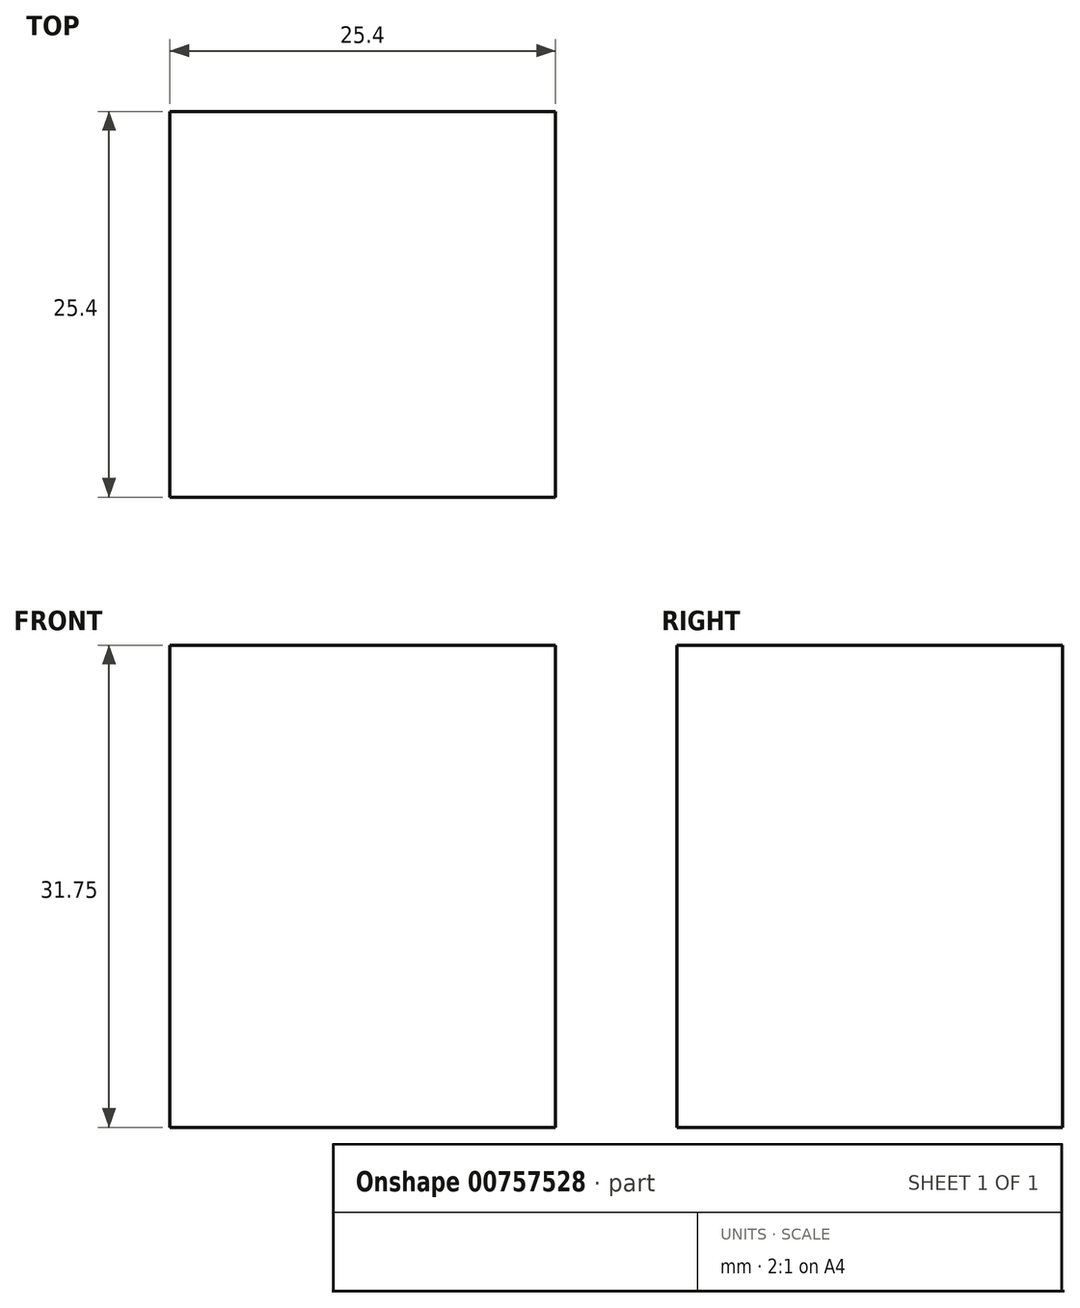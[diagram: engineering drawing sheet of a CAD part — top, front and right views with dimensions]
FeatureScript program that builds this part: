
annotation { "Feature Type Name" : "Feature", "Feature Type Description" : "" }
export const myFeature = defineFeature(function(context is Context, id is Id, definition is map)
    precondition{}
    {
        {
            var Q0;
            Q0=qCreatedBy(makeId("Right.planeOp"),FACE);
            var sketch = newSketch(context, id + "F0", { "sketchPlane" : qUnion([Q0])});
            skLineSegment(sketch, "E0", {"start": v(0, 31.75) * mm, "end": v(0, 0) * mm});
            skLineSegment(sketch, "E1", {"start": v(0, 0) * mm, "end": v(25.4, 0) * mm});
            skLineSegment(sketch, "E2", {"start": v(25.4, 0) * mm, "end": v(25.4, 31.75) * mm});
            skLineSegment(sketch, "E3", {"start": v(25.4, 31.75) * mm, "end": v(0, 31.75) * mm});
            skSolve(sketch);
        }
        {
            var Q0;
            Q0 = qSketchRegion(id + "F0", true);
            extrude(context, id + "F1", {"entities" : qUnion([Q0]), "depth" : 25.4 * mm, "offsetDistance" : 25.4 * mm});
        }
    });
